# Revit family: Sanitary_Toilets_hansgrohe_22466CHN-MitaPura-Original-S-Floorstanding-WC-Set_1-piece_Vertical-Outlet_305-rimless
name_source: partatom
category: Plumbing Fixtures
units: mm (PartAtom-declared; Revit-internal decimal feet)

## family parameters
Always vertical = No
Cut with Voids When Loaded = No
Maintain Annotation Orientation = No
OmniClass Number = 23.31.19.00
OmniClass Title = Toilets
Part Type = Normal
Room Calculation Point = No
Round Connector Dimension = Use Diameter
Shared = No
Work Plane-Based = Yes

## types (1)
- 007 White
    CW Connection = No
    CWFU = 0
    Connector Description = Water Outlet 102mm
    Cost = 0 $
    Default Elevation = 0 mm  [stored 0 ft]
    Description = MitaPura Original S Floorstanding WC Set one piece with vertical outlet 305 rimless
    Diameter = 102 mm
    HW Connection = No
    HWFU = 0
    Manufacturer = Hansgrohe
    Material 1 = Hansgrohe - White
    Material 2 = Hansgrohe - Metal - 007 Chrome
    Model = 22466CHN
    Product Page URL = https://www.hansgrohe.com
    Product data url = https://bimobject.com
    URL = https://www.hansgrohe.com
    Vent Connection = No
    Version = 1
    WFU = 0
    Waste Connection = No

note: [stored X ft] marks values corroborated as IEEE doubles in the binary element streams (Revit-internal decimal feet)

## geometry (parser evidence)
native form markers: Sweep x3
no freeform markers — native parametric forms only
